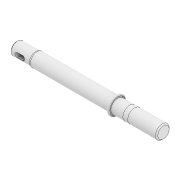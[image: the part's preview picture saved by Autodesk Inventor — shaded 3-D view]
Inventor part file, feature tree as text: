
AUTODESK INVENTOR PART (.ipt)
format: ipt  version: 2022 (Build 260153000, 153)  size: 182,784 bytes
history: native  units: mm
features: extrude x5, sketch x5, plane x2, fillet x2, projected_geometry x2, other x2, loft x1, chamfer x1
ambient origin geometry x8: Origin, YZ Plane, XZ Plane, XY Plane, X Axis, Y Axis, Z Axis, Center Point
bodies: Solid1 (feature_tree)
feature tree (20):
  extrude  "Shaft"  Depth=2.35mm TaperAngle=0.0deg
  extrude  "Slot for Differential Gear"  Depth=2.0mm
  plane  "Work Plane1"
  extrude  "Wheel Insert Profile"  Depth=7.0mm
  loft  "Loft1"
  plane  "Work Plane2"
  extrude  "Stopper"  Depth=7.5mm
  fillet  "Fillet1"  Radius=1.0mm
  extrude  "Differential Gear Insert Profile"  Depth=0.5mm
  fillet  "Fillet3"  Radius=3.0mm
  chamfer  "Chamfer4"  Distance=2.5mm
  sketch  "Sketch1"  dims[d2=0.0mm d9=2.35mm d10=0.0mm]
  sketch  "Sketch2"  dims[d17=1.8mm d20=2.0mm]
  sketch  "Sketch3"  dims[d21=1.0mm d22=7.0mm]
  sketch  "Sketch4"  dims[d25=12.0mm d26=0.0mm d29=2.0mm d32=0.0mm d33=90.0deg]
  projected_geometry  "Projected Loop1"
  other  "Edges2"
  other  "Edges4"
  sketch  "Sketch8"  dims[d34=-41.0mm d35=7.5mm d36=1.0mm d37=0.0mm d38=0.5mm d49=3.0mm d50=2.5mm d62=0.0mm d63=90.0deg d68=5.4mm d69=0.05mm d70=8.0mm d71=0.0mm d72=1.0mm d73=0.5mm d74=2.0mm d75=45.0deg]
  projected_geometry  "Project Cut Edges1"
